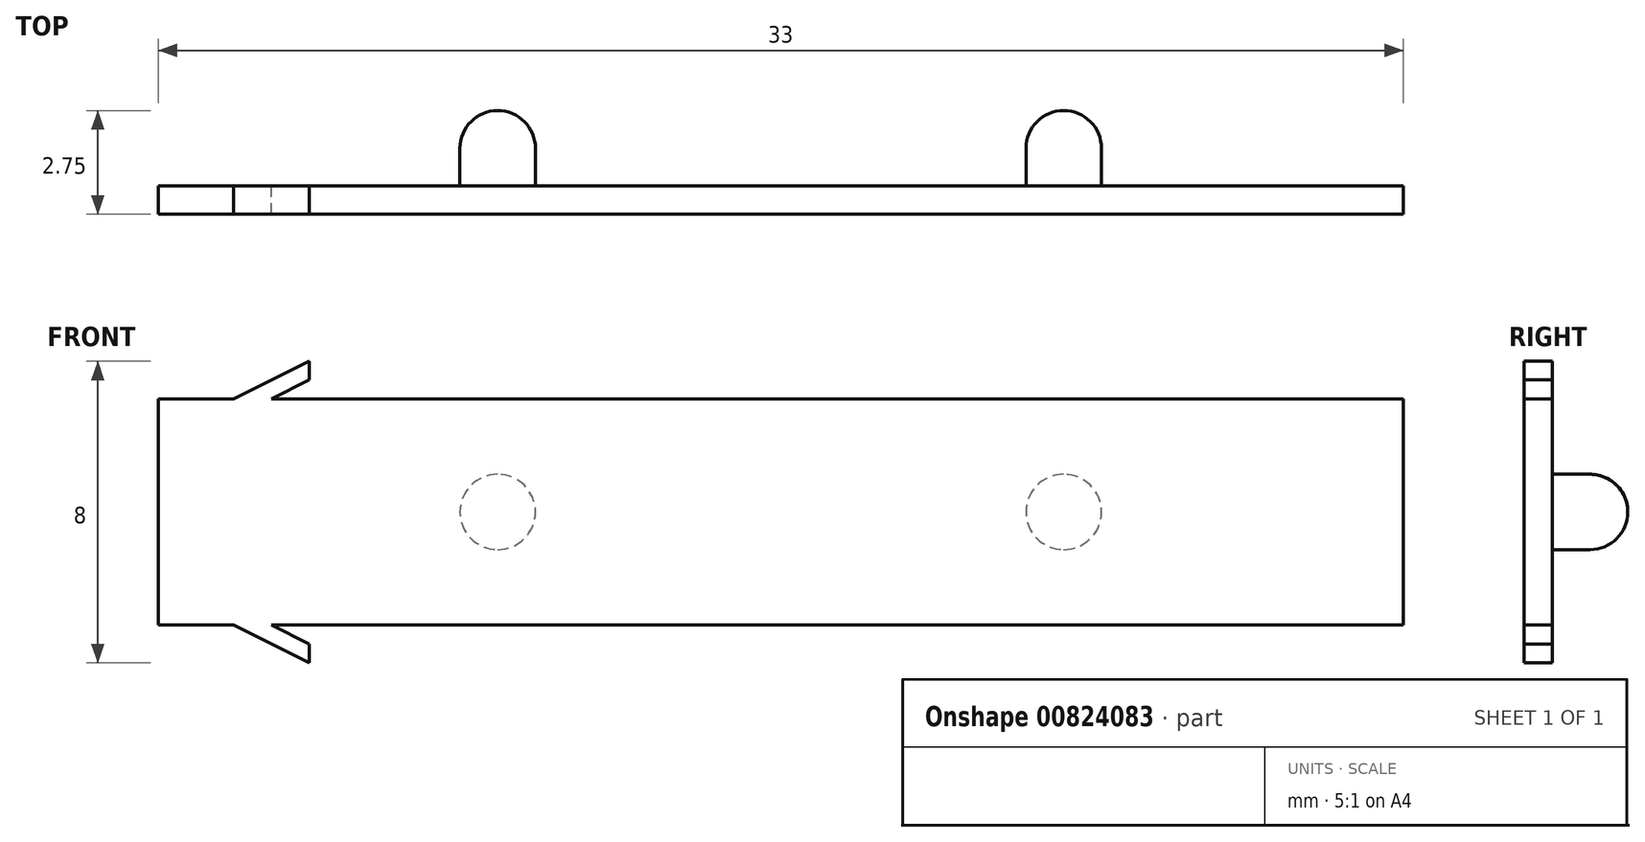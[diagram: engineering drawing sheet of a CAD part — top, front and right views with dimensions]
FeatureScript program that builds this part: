
annotation { "Feature Type Name" : "Feature", "Feature Type Description" : "" }
export const myFeature = defineFeature(function(context is Context, id is Id, definition is map)
    precondition{}
    {
        {
            var Q0;
            Q0=qCreatedBy(makeId("Right.planeOp"),FACE);
            var sketch = newSketch(context, id + "F0", { "sketchPlane" : qUnion([Q0])});
            skLineSegment(sketch, "E0.bottom", {"start": v(-9.14, 3.03) * mm, "end": v(-8.39, 3.03) * mm});
            skLineSegment(sketch, "E0.top", {"start": v(-9.14, -2.97) * mm, "end": v(-8.39, -2.97) * mm});
            skLineSegment(sketch, "E0.left", {"start": v(-9.14, 3.03) * mm, "end": v(-9.14, -2.97) * mm});
            skLineSegment(sketch, "E0.right", {"start": v(-8.39, 3.03) * mm, "end": v(-8.39, -2.97) * mm});
            skSolve(sketch);
        }
        {
            var Q0;
            Q0=makeQuery(id+"F0.imprint","IMPRINT",FACE,{"disambiguationData":[TD([[makeQuery(id+"F0.imprint","IMPRINT",EDGE,{"derivedFrom":sQuery(id+"F0.wireOp",EDGE,"E0.bottom")}),-1.0]])]});
            extrude(context, id + "F1", {"entities" : qUnion([Q0]), "depth" : 33 * mm, "offsetDistance" : 25 * mm});
        }
        {
            var Q0;
            Q0=makeQuery(id+"F1.opExtrude","SWEPT_FACE",FACE,{"disambiguationData":[OSD([sQuery(id+"F0.wireOp",EDGE,"E0.right")])]});
            var sketch = newSketch(context, id + "F2", { "sketchPlane" : qUnion([Q0])});
            skCircle(sketch, "E1", {"center": v(-9, 0.03) * mm, "radius": 1 * mm});
            skCircle(sketch, "E2", {"center": v(-24, 0.03) * mm, "radius": 1 * mm});
            skSolve(sketch);
        }
        {
            var Q0;
            Q0=makeQuery(id+"F2.imprint","IMPRINT",FACE,{"disambiguationData":[TD([[makeQuery(id+"F2.imprint","IMPRINT",EDGE,{"derivedFrom":sQuery(id+"F2.wireOp",EDGE,"E1")}),1.0]])]});
            var Q1;
            Q1=makeQuery(id+"F2.imprint","IMPRINT",FACE,{"disambiguationData":[TD([[makeQuery(id+"F2.imprint","IMPRINT",EDGE,{"derivedFrom":sQuery(id+"F2.wireOp",EDGE,"E2")}),1.0]])]});
            extrude(context, id + "F3", {"entities" : qUnion([Q0, Q1]), "operationType" : NewBodyOperationType.ADD, "depth" : 2 * mm, "offsetDistance" : 25 * mm});
        }
        {
            var Q0;
            Q0=makeQuery(id+"F3.opExtrude","CAP_EDGE",EDGE,{"disambiguationData":[OSD([sQuery(id+"F2.wireOp",EDGE,"E1")])],"isStart":false});
            var Q1;
            Q1=makeQuery(id+"F3.opExtrude","CAP_EDGE",EDGE,{"disambiguationData":[OSD([sQuery(id+"F2.wireOp",EDGE,"E2")])],"isStart":false});
            fillet(context, id + "F4", {"entities" : qUnion([Q0, Q1]), "radius" : 1 * mm, "tangentPropagation" : true, "allowEdgeOverflow" : false});
        }
        {
            var Q0;
            Q0=makeQuery(id+"F1.opExtrude","SWEPT_FACE",FACE,{"disambiguationData":[OSD([sQuery(id+"F0.wireOp",EDGE,"E0.bottom")])]});
            var sketch = newSketch(context, id + "F5", { "sketchPlane" : qUnion([Q0])});
            skLineSegment(sketch, "E3.bottom", {"start": v(2, -9.14) * mm, "end": v(4, -9.14) * mm});
            skLineSegment(sketch, "E3.top", {"start": v(2, -8.39) * mm, "end": v(4, -8.39) * mm});
            skLineSegment(sketch, "E3.left", {"start": v(2, -9.14) * mm, "end": v(2, -8.39) * mm});
            skLineSegment(sketch, "E3.right", {"start": v(4, -9.14) * mm, "end": v(4, -8.39) * mm});
            skSolve(sketch);
        }
        {
            var Q0;
            Q0 = qSketchRegion(id + "F5", true);
            extrude(context, id + "F6", {"entities" : qUnion([Q0]), "operationType" : NewBodyOperationType.ADD, "depth" : 1 * mm, "offsetDistance" : 25 * mm});
        }
        {
            var Q0;
            Q0=makeQuery(id+"F6.opExtrude","CAP_EDGE",EDGE,{"disambiguationData":[OSD([sQuery(id+"F5.wireOp",EDGE,"E3.left")])],"isStart":false});
            chamfer(context, id + "F7", {"entities" : qUnion([Q0]), "chamferType" : ChamferType.TWO_OFFSETS, "width1" : 1 * mm, "oppositeDirection" : false, "width2" : 2 * mm, "tangentPropagation" : true});
        }
        {
            var Q0;
            Q0=makeQuery(id+"F1.opExtrude","SWEPT_FACE",FACE,{"disambiguationData":[OSD([sQuery(id+"F0.wireOp",EDGE,"E0.top")])]});
            var sketch = newSketch(context, id + "F8", { "sketchPlane" : qUnion([Q0])});
            skLineSegment(sketch, "E4.bottom", {"start": v(2, 8.39) * mm, "end": v(4, 8.39) * mm});
            skLineSegment(sketch, "E4.top", {"start": v(2, 9.14) * mm, "end": v(4, 9.14) * mm});
            skLineSegment(sketch, "E4.left", {"start": v(2, 8.39) * mm, "end": v(2, 9.14) * mm});
            skLineSegment(sketch, "E4.right", {"start": v(4, 8.39) * mm, "end": v(4, 9.14) * mm});
            skSolve(sketch);
        }
        {
            var Q0;
            Q0=makeQuery(id+"F8.imprint","IMPRINT",FACE,{"disambiguationData":[TD([[makeQuery(id+"F8.imprint","IMPRINT",EDGE,{"derivedFrom":sQuery(id+"F8.wireOp",EDGE,"E4.bottom")}),-1.0]])]});
            extrude(context, id + "F9", {"entities" : qUnion([Q0]), "operationType" : NewBodyOperationType.ADD, "depth" : 1 * mm, "offsetDistance" : 25 * mm});
        }
        {
            var Q0;
            Q0=makeQuery(id+"F9.opExtrude","CAP_EDGE",EDGE,{"disambiguationData":[OSD([sQuery(id+"F8.wireOp",EDGE,"E4.left")])],"isStart":false});
            chamfer(context, id + "F10", {"entities" : qUnion([Q0]), "chamferType" : ChamferType.TWO_OFFSETS, "width1" : 1 * mm, "oppositeDirection" : false, "width2" : 2 * mm, "tangentPropagation" : true});
        }
        {
            var Q0;
            Q0=makeQuery(id+"F9.boolean.opBoolean","MERGE",FACE,{"derivedFrom":[makeQuery(id+"F6.boolean.opBoolean","MERGE",FACE,{"derivedFrom":[makeQuery(id+"F1.opExtrude","SWEPT_FACE",FACE,{"disambiguationData":[OSD([sQuery(id+"F0.wireOp",EDGE,"E0.right")])]}),makeQuery(id+"F6.opExtrude","SWEPT_FACE",FACE,{"disambiguationData":[OSD([sQuery(id+"F5.wireOp",EDGE,"E3.top")])]})]}),makeQuery(id+"F9.opExtrude","SWEPT_FACE",FACE,{"disambiguationData":[OSD([sQuery(id+"F8.wireOp",EDGE,"E4.bottom")])]})]});
            var sketch = newSketch(context, id + "F11", { "sketchPlane" : qUnion([Q0])});
            skLineSegment(sketch, "E5", {"start": v(-4, 3.53) * mm, "end": v(-3, 3.03) * mm});
            skLineSegment(sketch, "E6", {"start": v(-3, 3.03) * mm, "end": v(-4, 3.03) * mm});
            skLineSegment(sketch, "E7", {"start": v(-4, 3.03) * mm, "end": v(-4, 3.53) * mm});
            skLineSegment(sketch, "E8", {"start": v(-4, -2.97) * mm, "end": v(-3, -2.97) * mm});
            skLineSegment(sketch, "E9", {"start": v(-3, -2.97) * mm, "end": v(-4, -3.47) * mm});
            skLineSegment(sketch, "E10", {"start": v(-4, -2.97) * mm, "end": v(-4, -3.47) * mm});
            skSolve(sketch);
        }
        {
            var Q0;
            Q0 = qSketchRegion(id + "F11", true);
            extrude(context, id + "F12", {"entities" : qUnion([Q0]), "operationType" : NewBodyOperationType.REMOVE, "oppositeDirection" : true, "depth" : 25 * mm, "offsetDistance" : 25 * mm});
        }
    });
